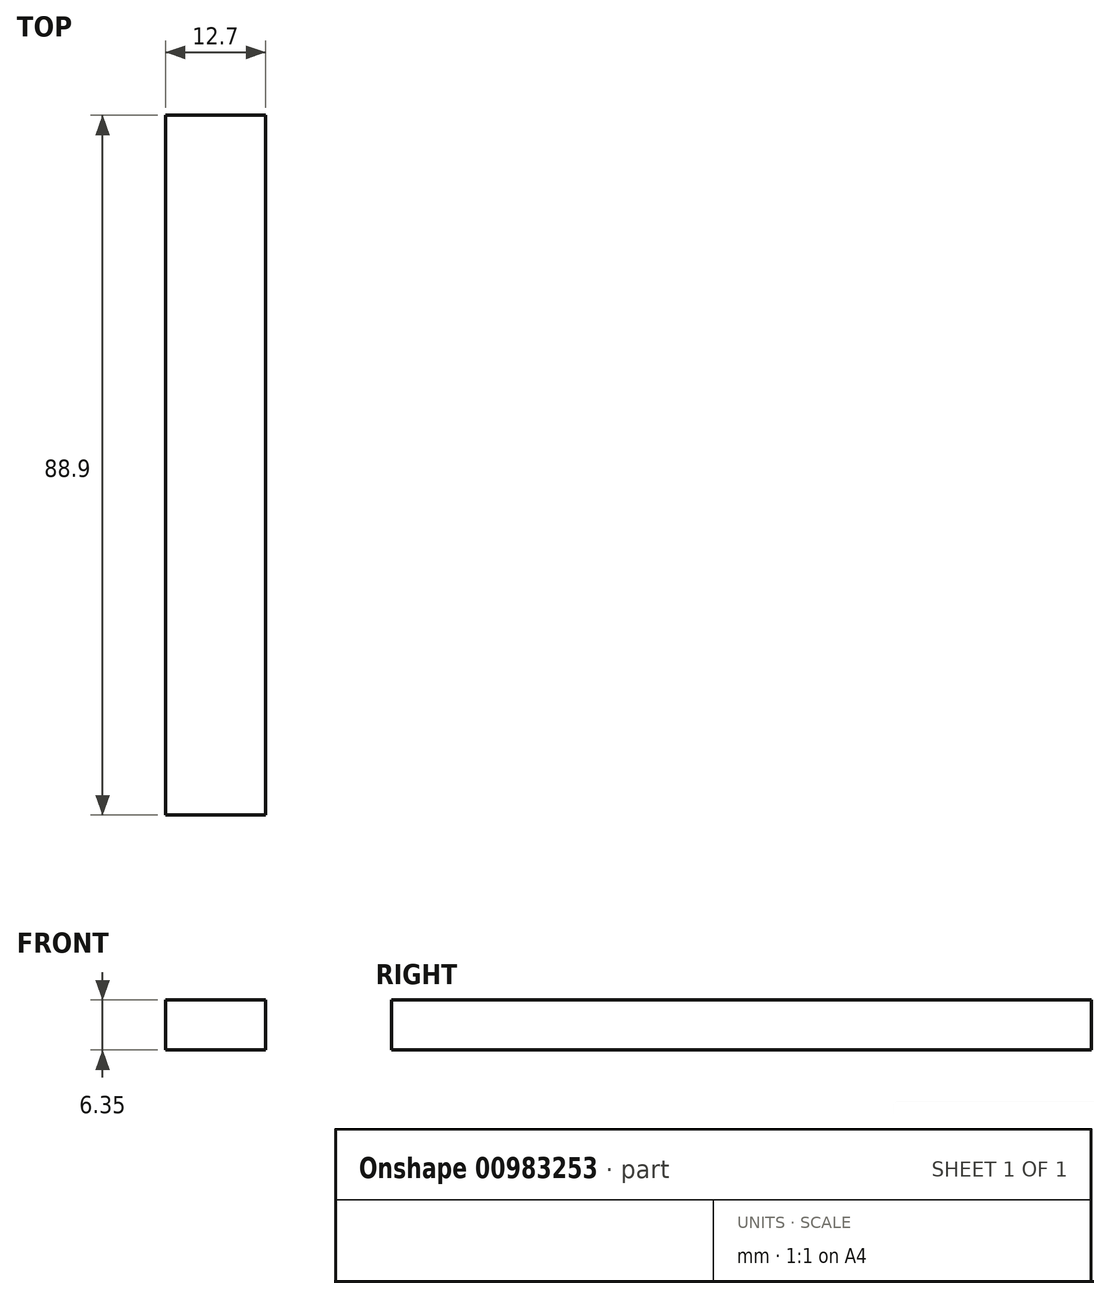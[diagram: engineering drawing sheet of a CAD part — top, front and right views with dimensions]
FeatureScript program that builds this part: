
annotation { "Feature Type Name" : "Feature", "Feature Type Description" : "" }
export const myFeature = defineFeature(function(context is Context, id is Id, definition is map)
    precondition{}
    {
        {
            var Q0;
            Q0=qCreatedBy(makeId("Top.planeOp"),FACE);
            var sketch = newSketch(context, id + "F0", { "sketchPlane" : qUnion([Q0])});
            skLineSegment(sketch, "E0.bottom", {"start": v(6.35, 44.45) * mm, "end": v(-6.35, 44.45) * mm});
            skLineSegment(sketch, "E0.top", {"start": v(6.35, -44.45) * mm, "end": v(-6.35, -44.45) * mm});
            skLineSegment(sketch, "E0.left", {"start": v(6.35, 44.45) * mm, "end": v(6.35, -44.45) * mm});
            skLineSegment(sketch, "E0.right", {"start": v(-6.35, 44.45) * mm, "end": v(-6.35, -44.45) * mm});
            skPoint(sketch, "E0.middle", {"position": v(0, 0) * mm});
            skSolve(sketch);
        }
        {
            var Q0;
            Q0=makeQuery(id+"F0.imprint","IMPRINT",FACE,{"disambiguationData":[TD([[makeQuery(id+"F0.imprint","IMPRINT",EDGE,{"derivedFrom":sQuery(id+"F0.wireOp",EDGE,"E0.bottom")}),1.0]])]});
            extrude(context, id + "F1", {"entities" : qUnion([Q0]), "depth" : 6.35 * mm, "offsetDistance" : 25.4 * mm});
        }
    });
